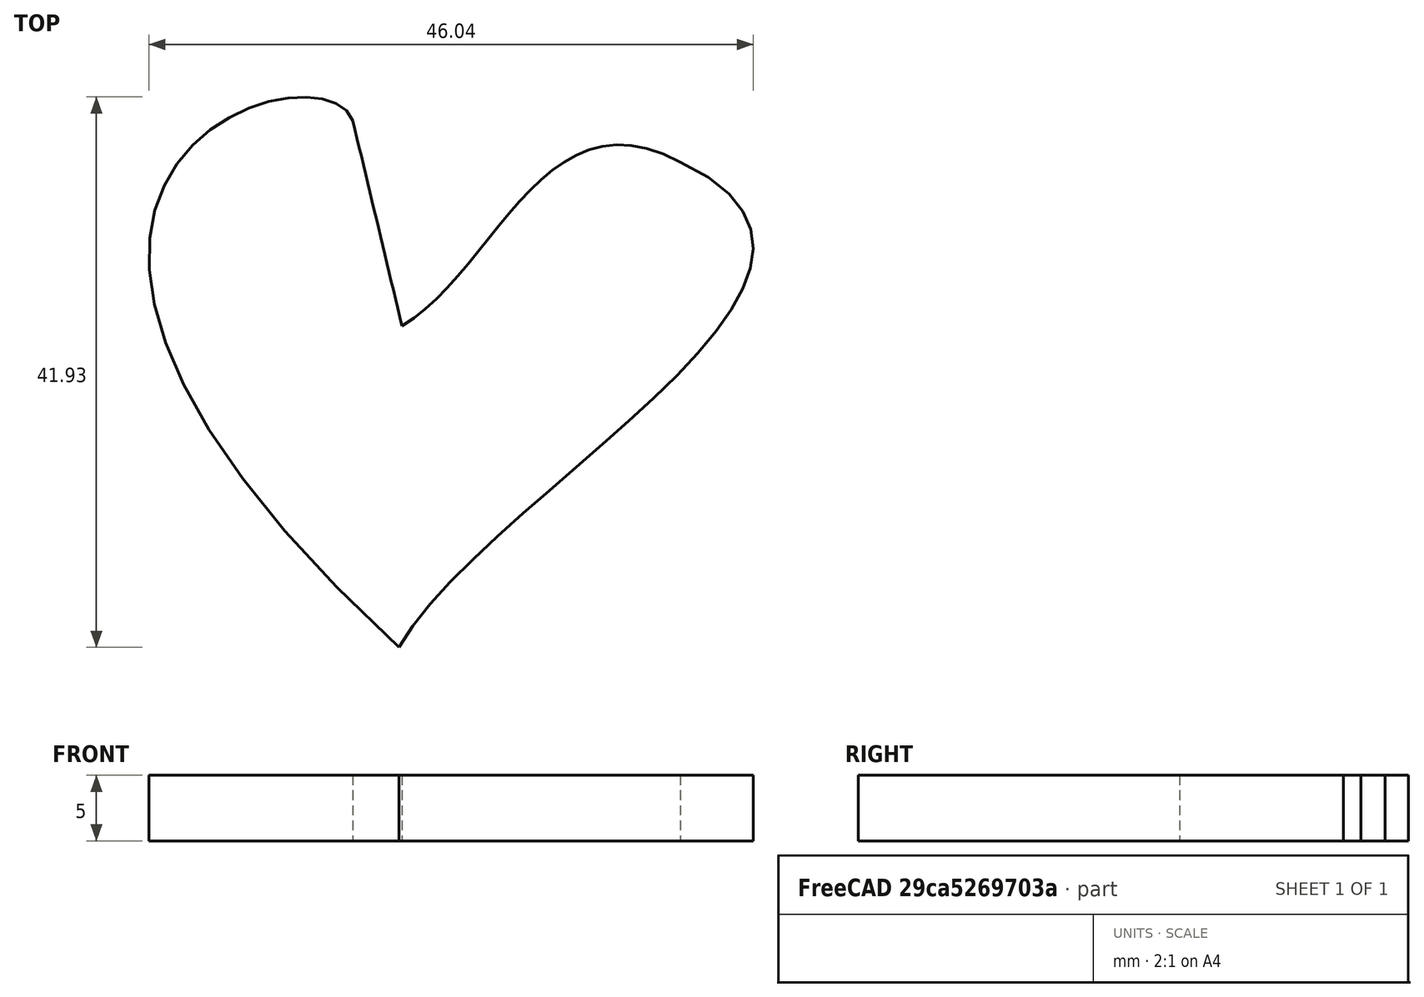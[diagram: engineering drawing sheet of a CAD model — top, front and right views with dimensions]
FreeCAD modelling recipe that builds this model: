
FCSTD DOCUMENT  (FreeCAD 1.0R38806 (Git))
Label: cutre-corazon
License: All rights reserved
LicenseURL: https://en.wikipedia.org/wiki/All_rights_reserved
objects: Part::Feature×1, Part::Extrusion×1, Part::Cylinder×1, Part::Cut×1
note: 4 computed .brp shape members not serialized (recipe doc carries the construction recipe); baked Part::Feature solids carry a one-line shape summary decoded from their .brp

FEATURE [Part::Feature] path1  label="boceto-corazon"
  shape: bbox 58.09 x 46.57 x 2e-07 mm, 0 faces, 0 solids (baked)
FEATURE [Part::Extrusion] Extrude  label="Corazon"
  Base = -> path1
  Dir = (0,0,-1)
  DirMode = 2
  FaceMakerClass = Part::FaceMakerBullseye
  FaceMakerMode = 3
  LengthFwd = 5
  LengthRev = 0
  Solid = true
  Symmetric = false
FEATURE [Part::Cylinder] Cylinder
  Angle = 360
  AttacherType = Attacher::AttachEngine3D
  FirstAngle = 0
  Height = 10
  Placement = pos=(116,-84,0) rot=(0,0,1;0rad)
  Radius = 2
  SecondAngle = 0
FEATURE [Part::Cut] Cut
  Base = -> Extrude
  Tool = -> Cylinder
